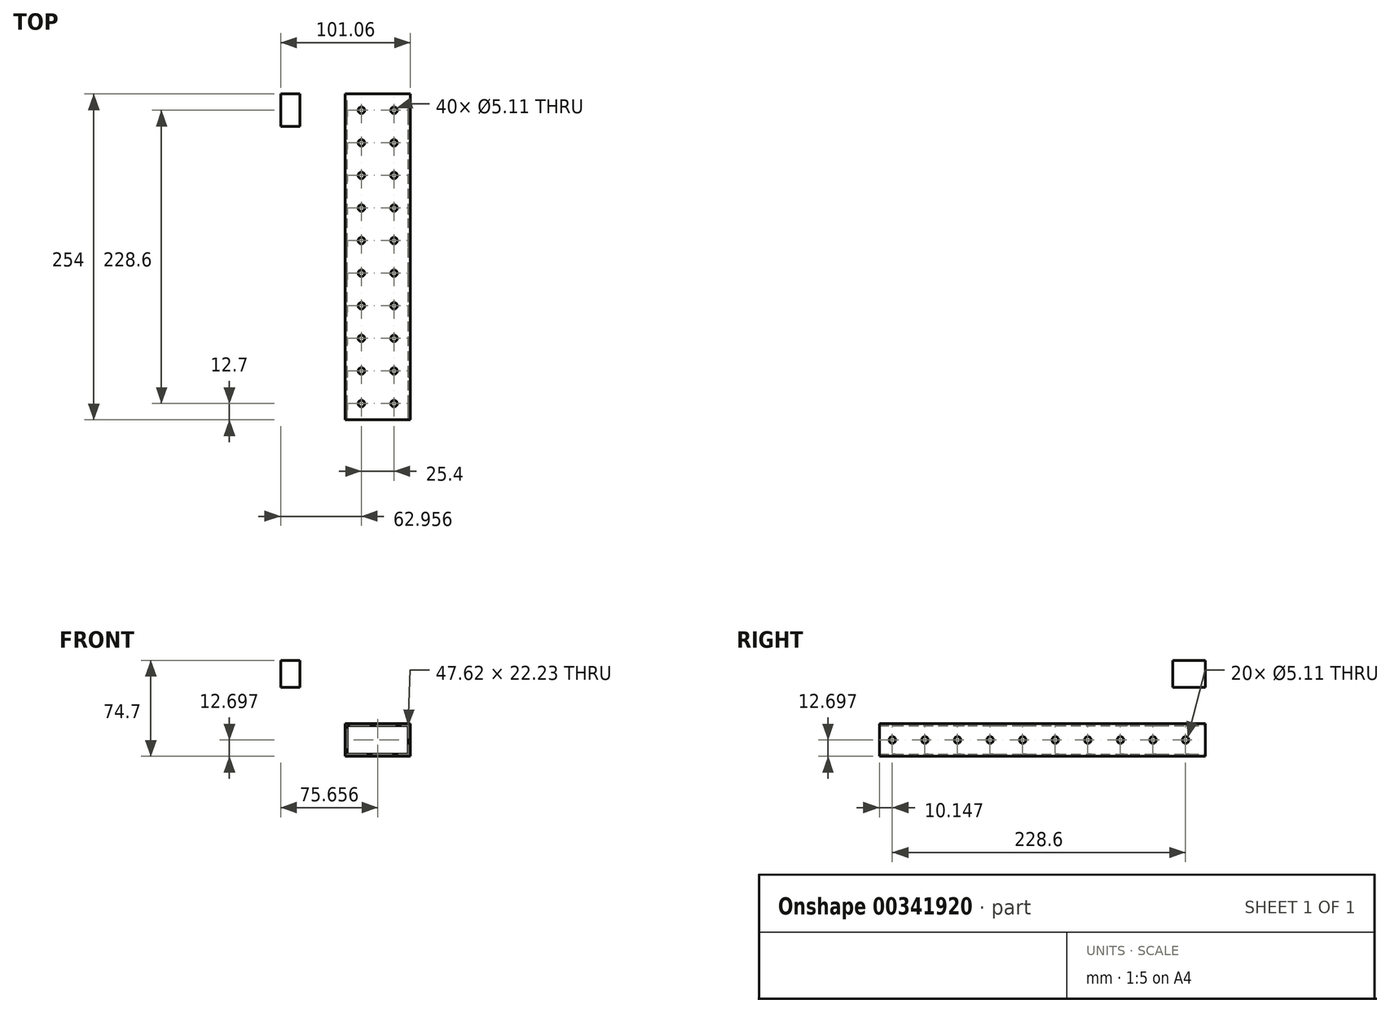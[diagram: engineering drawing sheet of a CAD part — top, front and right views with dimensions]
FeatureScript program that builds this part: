
annotation { "Feature Type Name" : "Feature", "Feature Type Description" : "" }
export const myFeature = defineFeature(function(context is Context, id is Id, definition is map)
    precondition{}
    {
        {
            var Q0;
            Q0=qCreatedBy(makeId("Front.planeOp"),FACE);
            var sketch = newSketch(context, id + "F0", { "sketchPlane" : qUnion([Q0])});
            skLineSegment(sketch, "E0.bottom", {"start": v(-15.94, 6.36) * mm, "end": v(34.86, 6.36) * mm});
            skLineSegment(sketch, "E0.top", {"start": v(-15.94, -19.04) * mm, "end": v(34.86, -19.04) * mm});
            skLineSegment(sketch, "E0.left", {"start": v(-15.94, 6.36) * mm, "end": v(-15.94, -19.04) * mm});
            skLineSegment(sketch, "E0.right", {"start": v(34.86, 6.36) * mm, "end": v(34.86, -19.04) * mm});
            skLineSegment(sketch, "E1.bottom", {"start": v(-14.36, -17.46) * mm, "end": v(33.27, -17.46) * mm});
            skLineSegment(sketch, "E1.top", {"start": v(-14.36, 4.77) * mm, "end": v(33.27, 4.77) * mm});
            skLineSegment(sketch, "E1.left", {"start": v(-14.36, -17.46) * mm, "end": v(-14.36, 4.77) * mm});
            skLineSegment(sketch, "E1.right", {"start": v(33.27, -17.46) * mm, "end": v(33.27, 4.77) * mm});
            skSolve(sketch);
        }
        {
            var Q0;
            Q0=makeQuery(id+"F0.imprint","IMPRINT",FACE,{"disambiguationData":[TD([[makeQuery(id+"F0.imprint","IMPRINT",EDGE,{"derivedFrom":sQuery(id+"F0.wireOp",EDGE,"E0.bottom")}),-1.0]])]});
            var Q1;
            Q1 = qSketchRegion(id + "F2", true);
            extrude(context, id + "F1", {"entities" : qUnion([Q0, Q1]), "depth" : 254 * mm});
        }
        {
            var Q0;
            Q0=makeQuery(id+"F1.opExtrude","SWEPT_FACE",FACE,{"disambiguationData":[OSD([sQuery(id+"F0.wireOp",EDGE,"E0.left")])]});
            var sketch = newSketch(context, id + "F2", { "sketchPlane" : qUnion([Q0])});
            skCircle(sketch, "E2", {"center": v(15.25, -6.34) * mm, "radius": 2.55 * mm});
            skCircle(sketch, "E3.1.0.0", {"center": v(40.65, -6.34) * mm, "radius": 2.55 * mm});
            skCircle(sketch, "E3.2.0.0", {"center": v(66.05, -6.34) * mm, "radius": 2.55 * mm});
            skCircle(sketch, "E3.3.0.0", {"center": v(91.45, -6.34) * mm, "radius": 2.55 * mm});
            skCircle(sketch, "E3.4.0.0", {"center": v(116.85, -6.34) * mm, "radius": 2.55 * mm});
            skCircle(sketch, "E3.5.0.0", {"center": v(142.25, -6.34) * mm, "radius": 2.55 * mm});
            skCircle(sketch, "E3.6.0.0", {"center": v(167.65, -6.34) * mm, "radius": 2.55 * mm});
            skCircle(sketch, "E3.7.0.0", {"center": v(193.05, -6.34) * mm, "radius": 2.55 * mm});
            skCircle(sketch, "E3.8.0.0", {"center": v(218.45, -6.34) * mm, "radius": 2.55 * mm});
            skCircle(sketch, "E3.9.0.0", {"center": v(243.85, -6.34) * mm, "radius": 2.55 * mm});
            skLineSegment(sketch, "E3.direction1", {"start": v(15.25, -6.34) * mm, "end": v(40.65, -6.34) * mm, "construction": true});
            skSolve(sketch);
        }
        {
            var Q0;
            Q0=sQuery(id+"F2.wireOp",VERTEX,"E3.1.0.0.center");
            var Q1;
            Q1=sQuery(id+"F2.wireOp",VERTEX,"E3.2.0.0.center");
            var Q2;
            Q2=sQuery(id+"F2.wireOp",VERTEX,"E3.3.0.0.center");
            var Q3;
            Q3=sQuery(id+"F2.wireOp",VERTEX,"E3.4.0.0.center");
            var Q4;
            Q4=sQuery(id+"F2.wireOp",VERTEX,"E3.direction1.start");
            var Q5;
            Q5=sQuery(id+"F2.wireOp",VERTEX,"E3.5.0.0.center");
            var Q6;
            Q6=sQuery(id+"F2.wireOp",VERTEX,"E3.6.0.0.center");
            var Q7;
            Q7=sQuery(id+"F2.wireOp",VERTEX,"E3.7.0.0.center");
            var Q8;
            Q8=sQuery(id+"F2.wireOp",VERTEX,"E3.8.0.0.center");
            var Q9;
            Q9=sQuery(id+"F2.wireOp",VERTEX,"E3.9.0.0.center");
            var Q10;
            Q10=makeQuery(id+"F1.opExtrude","SWEPT_BODY",BODY,{"disambiguationData":[OSD([sQuery(id+"F0.wireOp",EDGE,"E0.bottom"),sQuery(id+"F0.wireOp",EDGE,"E0.top"),sQuery(id+"F0.wireOp",EDGE,"E0.left"),sQuery(id+"F0.wireOp",EDGE,"E0.right"),sQuery(id+"F0.wireOp",EDGE,"E1.bottom"),sQuery(id+"F0.wireOp",EDGE,"E1.top"),sQuery(id+"F0.wireOp",EDGE,"E1.left"),sQuery(id+"F0.wireOp",EDGE,"E1.right")])]});
            hole(context, id + "F3", {"style" : HoleStyle.SIMPLE, "endStyle" : HoleEndStyle.THROUGH, "holeDiameter" : 5.1 * mm, "isTappedThrough" : true, "tappedDepth" : 12.7 * mm, "tapClearance" : 3, "locations" : qUnion([Q0, Q1, Q2, Q3, Q4, Q5, Q6, Q7, Q8, Q9]), "scope" : qUnion([Q10])});
        }
        {
            var Q0;
            Q0=makeQuery(id+"F1.opExtrude","SWEPT_FACE",FACE,{"disambiguationData":[OSD([sQuery(id+"F0.wireOp",EDGE,"E0.top")])]});
            var sketch = newSketch(context, id + "F4", { "sketchPlane" : qUnion([Q0])});
            skCircle(sketch, "E4", {"center": v(-3.24, 12.7) * mm, "radius": 2.55 * mm});
            skCircle(sketch, "E5.0.1.0", {"center": v(-3.24, 38.1) * mm, "radius": 2.55 * mm});
            skCircle(sketch, "E5.0.2.0", {"center": v(-3.24, 63.5) * mm, "radius": 2.55 * mm});
            skCircle(sketch, "E5.0.3.0", {"center": v(-3.24, 88.9) * mm, "radius": 2.55 * mm});
            skCircle(sketch, "E5.0.4.0", {"center": v(-3.24, 114.3) * mm, "radius": 2.55 * mm});
            skCircle(sketch, "E5.0.5.0", {"center": v(-3.24, 139.7) * mm, "radius": 2.55 * mm});
            skCircle(sketch, "E5.0.6.0", {"center": v(-3.24, 165.1) * mm, "radius": 2.55 * mm});
            skCircle(sketch, "E5.0.7.0", {"center": v(-3.24, 190.5) * mm, "radius": 2.55 * mm});
            skCircle(sketch, "E5.0.8.0", {"center": v(-3.24, 215.9) * mm, "radius": 2.55 * mm});
            skCircle(sketch, "E5.0.9.0", {"center": v(-3.24, 241.3) * mm, "radius": 2.55 * mm});
            skCircle(sketch, "E5.1.0.0", {"center": v(22.16, 12.7) * mm, "radius": 2.55 * mm});
            skCircle(sketch, "E5.1.1.0", {"center": v(22.16, 38.1) * mm, "radius": 2.55 * mm});
            skCircle(sketch, "E5.1.2.0", {"center": v(22.16, 63.5) * mm, "radius": 2.55 * mm});
            skCircle(sketch, "E5.1.3.0", {"center": v(22.16, 88.9) * mm, "radius": 2.55 * mm});
            skCircle(sketch, "E5.1.4.0", {"center": v(22.16, 114.3) * mm, "radius": 2.55 * mm});
            skCircle(sketch, "E5.1.5.0", {"center": v(22.16, 139.7) * mm, "radius": 2.55 * mm});
            skCircle(sketch, "E5.1.6.0", {"center": v(22.16, 165.1) * mm, "radius": 2.55 * mm});
            skCircle(sketch, "E5.1.7.0", {"center": v(22.16, 190.5) * mm, "radius": 2.55 * mm});
            skCircle(sketch, "E5.1.8.0", {"center": v(22.16, 215.9) * mm, "radius": 2.55 * mm});
            skCircle(sketch, "E5.1.9.0", {"center": v(22.16, 241.3) * mm, "radius": 2.55 * mm});
            skLineSegment(sketch, "E5.direction1", {"start": v(-3.24, 12.7) * mm, "end": v(22.16, 12.7) * mm, "construction": true});
            skLineSegment(sketch, "E5.direction2", {"start": v(-3.24, 12.7) * mm, "end": v(-3.24, 38.1) * mm, "construction": true});
            skSolve(sketch);
        }
        {
            var Q0;
            Q0=sQuery(id+"F4.wireOp",VERTEX,"E5.direction2.start");
            var Q1;
            Q1=sQuery(id+"F4.wireOp",VERTEX,"E5.direction1.end");
            var Q2;
            Q2=sQuery(id+"F4.wireOp",VERTEX,"E5.1.1.0.center");
            var Q3;
            Q3=sQuery(id+"F4.wireOp",VERTEX,"E5.direction2.end");
            var Q4;
            Q4=sQuery(id+"F4.wireOp",VERTEX,"E5.1.2.0.center");
            var Q5;
            Q5=sQuery(id+"F4.wireOp",VERTEX,"E5.0.2.0.center");
            var Q6;
            Q6=sQuery(id+"F4.wireOp",VERTEX,"E5.1.3.0.center");
            var Q7;
            Q7=sQuery(id+"F4.wireOp",VERTEX,"E5.0.3.0.center");
            var Q8;
            Q8=sQuery(id+"F4.wireOp",VERTEX,"E5.1.4.0.center");
            var Q9;
            Q9=sQuery(id+"F4.wireOp",VERTEX,"E5.0.4.0.center");
            var Q10;
            Q10=sQuery(id+"F4.wireOp",VERTEX,"E5.1.5.0.center");
            var Q11;
            Q11=sQuery(id+"F4.wireOp",VERTEX,"E5.0.5.0.center");
            var Q12;
            Q12=sQuery(id+"F4.wireOp",VERTEX,"E5.1.6.0.center");
            var Q13;
            Q13=sQuery(id+"F4.wireOp",VERTEX,"E5.0.6.0.center");
            var Q14;
            Q14=sQuery(id+"F4.wireOp",VERTEX,"E5.1.7.0.center");
            var Q15;
            Q15=sQuery(id+"F4.wireOp",VERTEX,"E5.0.7.0.center");
            var Q16;
            Q16=sQuery(id+"F4.wireOp",VERTEX,"E5.1.8.0.center");
            var Q17;
            Q17=sQuery(id+"F4.wireOp",VERTEX,"E5.0.8.0.center");
            var Q18;
            Q18=sQuery(id+"F4.wireOp",VERTEX,"E5.1.9.0.center");
            var Q19;
            Q19=sQuery(id+"F4.wireOp",VERTEX,"E5.0.9.0.center");
            var Q20;
            Q20=makeQuery(id+"F1.opExtrude","SWEPT_BODY",BODY,{"disambiguationData":[OSD([sQuery(id+"F0.wireOp",EDGE,"E0.bottom"),sQuery(id+"F0.wireOp",EDGE,"E0.top"),sQuery(id+"F0.wireOp",EDGE,"E0.left"),sQuery(id+"F0.wireOp",EDGE,"E0.right"),sQuery(id+"F0.wireOp",EDGE,"E1.bottom"),sQuery(id+"F0.wireOp",EDGE,"E1.top"),sQuery(id+"F0.wireOp",EDGE,"E1.left"),sQuery(id+"F0.wireOp",EDGE,"E1.right")])]});
            hole(context, id + "F5", {"style" : HoleStyle.SIMPLE, "endStyle" : HoleEndStyle.THROUGH, "holeDiameter" : 5.1 * mm, "isTappedThrough" : true, "tappedDepth" : 12.7 * mm, "tapClearance" : 3, "locations" : qUnion([Q0, Q1, Q2, Q3, Q4, Q5, Q6, Q7, Q8, Q9, Q10, Q11, Q12, Q13, Q14, Q15, Q16, Q17, Q18, Q19]), "scope" : qUnion([Q20])});
        }
        {
            var Q0;
            Q0=qCreatedBy(makeId("Front.planeOp"),FACE);
            var sketch = newSketch(context, id + "F6", { "sketchPlane" : qUnion([Q0])});
            skLineSegment(sketch, "E6.bottom", {"start": v(-66.2, 55.66) * mm, "end": v(-51.32, 55.66) * mm});
            skLineSegment(sketch, "E6.top", {"start": v(-66.2, 34.73) * mm, "end": v(-51.32, 34.73) * mm});
            skLineSegment(sketch, "E6.left", {"start": v(-66.2, 55.66) * mm, "end": v(-66.2, 34.73) * mm});
            skLineSegment(sketch, "E6.right", {"start": v(-51.32, 55.66) * mm, "end": v(-51.32, 34.73) * mm});
            skSolve(sketch);
        }
        {
            var Q0;
            Q0=makeQuery(id+"F6.imprint","IMPRINT",FACE,{"disambiguationData":[TD([[makeQuery(id+"F6.imprint","IMPRINT",EDGE,{"derivedFrom":sQuery(id+"F6.wireOp",EDGE,"E6.bottom")}),-1.0]])]});
            extrude(context, id + "F7", {"entities" : qUnion([Q0]), "depth" : 25.4 * mm});
        }
    });
